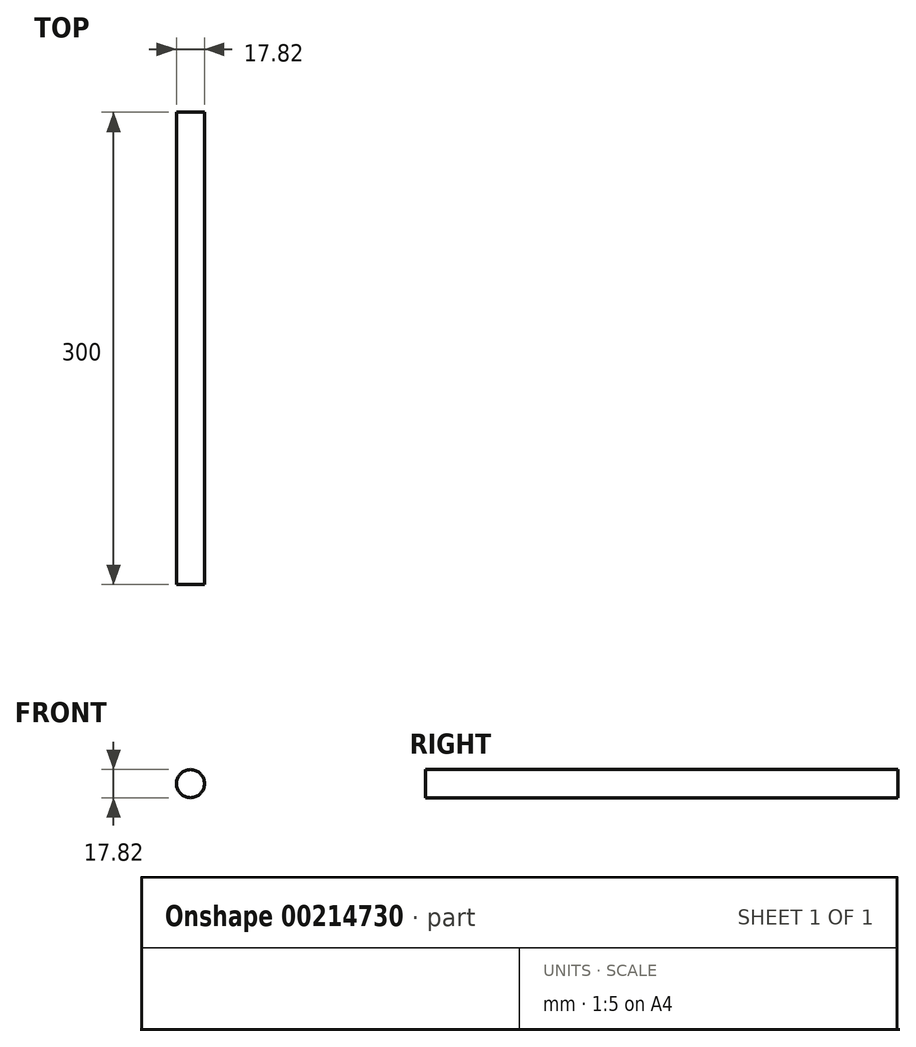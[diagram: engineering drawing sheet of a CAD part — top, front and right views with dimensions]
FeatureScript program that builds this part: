
annotation { "Feature Type Name" : "Feature", "Feature Type Description" : "" }
export const myFeature = defineFeature(function(context is Context, id is Id, definition is map)
    precondition{}
    {
        {
            var Q0;
            Q0=qCreatedBy(makeId("Front.planeOp"),FACE);
            var sketch = newSketch(context, id + "F0", { "sketchPlane" : qUnion([Q0])});
            skCircle(sketch, "E0", {"center": v(0, 0) * mm, "radius": 8.9 * mm});
            skSolve(sketch);
        }
        {
            var Q0;
            Q0=makeQuery(id+"F0.imprint","IMPRINT",FACE,{"disambiguationData":[TD([[makeQuery(id+"F0.imprint","IMPRINT",EDGE,{"derivedFrom":sQuery(id+"F0.wireOp",EDGE,"E0")}),1.0]])]});
            extrude(context, id + "F1", {"entities" : qUnion([Q0]), "depth" : 300 * mm});
        }
    });
